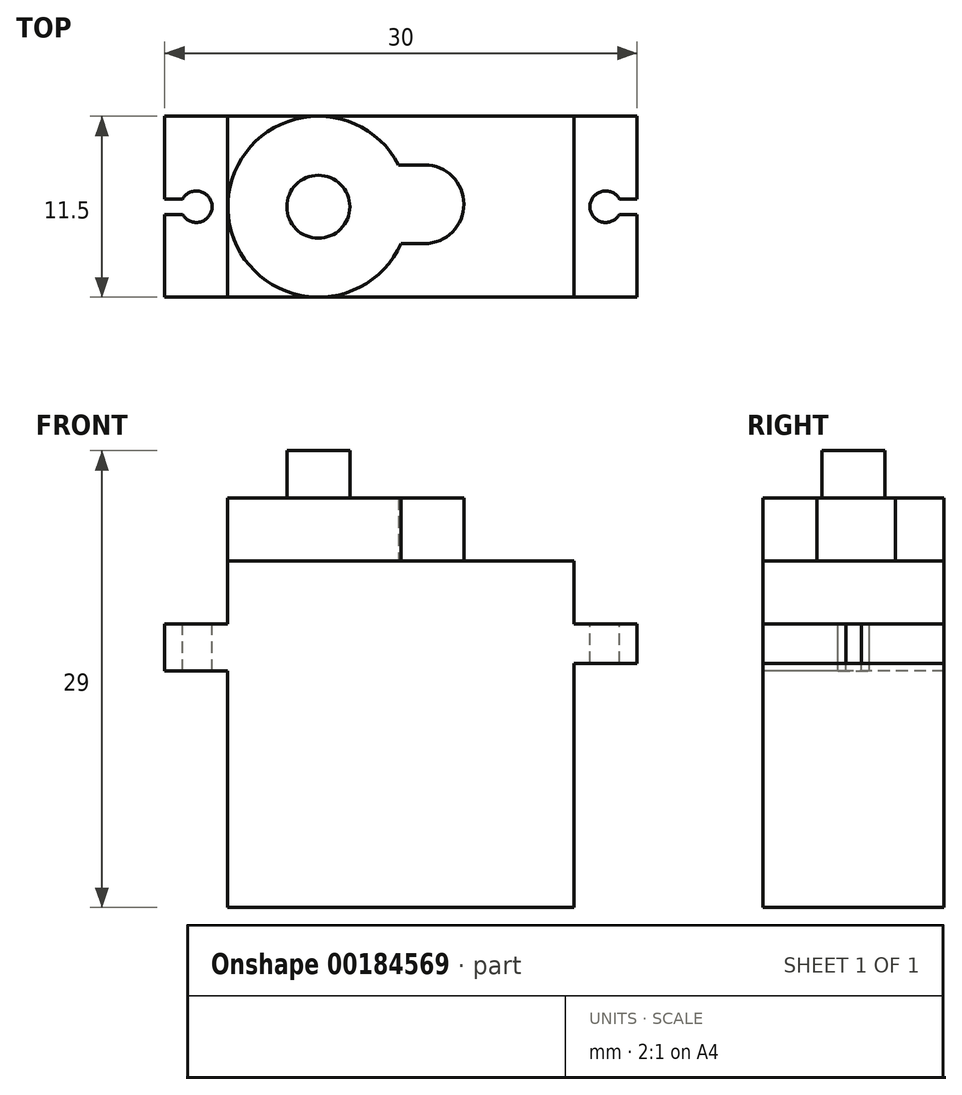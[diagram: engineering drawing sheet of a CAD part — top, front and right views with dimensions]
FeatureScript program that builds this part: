
annotation { "Feature Type Name" : "Feature", "Feature Type Description" : "" }
export const myFeature = defineFeature(function(context is Context, id is Id, definition is map)
    precondition{}
    {
        {
            var Q0;
            Q0=qCreatedBy(makeId("Front.planeOp"),FACE);
            var sketch = newSketch(context, id + "F0", { "sketchPlane" : qUnion([Q0])});
            skLineSegment(sketch, "E0.bottom", {"start": v(0, 0) * mm, "end": v(-22, 0) * mm});
            skLineSegment(sketch, "E0.top", {"start": v(0, 22) * mm, "end": v(-22, 22) * mm});
            skLineSegment(sketch, "E0.left", {"start": v(0, 0) * mm, "end": v(0, 22) * mm});
            skLineSegment(sketch, "E0.right", {"start": v(-22, 0) * mm, "end": v(-22, 22) * mm});
            skSolve(sketch);
        }
        {
            var Q0;
            Q0=makeQuery(id+"F0.imprint","IMPRINT",FACE,{"disambiguationData":[TD([[makeQuery(id+"F0.imprint","IMPRINT",EDGE,{"derivedFrom":sQuery(id+"F0.wireOp",EDGE,"E0.bottom")}),-1.0]])]});
            extrude(context, id + "F1", {"entities" : qUnion([Q0]), "depth" : 11.5 * mm});
        }
        {
            var Q0;
            Q0=makeQuery(id+"F1.opExtrude","SWEPT_FACE",FACE,{"disambiguationData":[OSD([sQuery(id+"F0.wireOp",EDGE,"E0.top")])]});
            var sketch = newSketch(context, id + "F2", { "sketchPlane" : qUnion([Q0])});
            skCircle(sketch, "E1", {"center": v(-16.25, -5.75) * mm, "radius": 5.75 * mm});
            skCircle(sketch, "E2", {"center": v(-9.5, -5.59) * mm, "radius": 2.5 * mm});
            skLineSegment(sketch, "E3", {"start": v(-9.5, -3.09) * mm, "end": v(-11.15, -3.09) * mm});
            skLineSegment(sketch, "E4", {"start": v(-9.5, -8.09) * mm, "end": v(-11, -8.09) * mm});
            skSolve(sketch);
        }
        {
            var Q0;
            {var subQ0=sQuery(id+"F2.wireOp",EDGE,"E1");var subQ5=makeQuery(id+"F2.imprint","INTERSECT",VERTEX,{"derivedFrom":[subQ0,sQuery(id+"F2.wireOp",EDGE,"E3")]});Q0=makeQuery(id+"F2.imprint","IMPRINT",FACE,{"disambiguationData":[TD([[makeQuery(id+"F2.imprint","IMPRINT",EDGE,{"disambiguationData":[TD([[subQ5,1.0]])],"derivedFrom":subQ0}),1.0]])]});}
            var Q1;
            {var subQ0=sQuery(id+"F2.wireOp",EDGE,"E2");var subQ1=sQuery(id+"F2.wireOp",EDGE,"E1");var subQ2=makeQuery(id+"F2.imprint","INTERSECT",VERTEX,{"disambiguationData":[OD(0.0)],"derivedFrom":[subQ1,subQ0]});Q1=makeQuery(id+"F2.imprint","IMPRINT",FACE,{"disambiguationData":[TD([[makeQuery(id+"F2.imprint","IMPRINT",EDGE,{"disambiguationData":[TD([[subQ2,1.0]])],"derivedFrom":subQ1}),1.0]])]});}
            var Q2;
            {var subQ0=sQuery(id+"F2.wireOp",EDGE,"E2");var subQ1=sQuery(id+"F2.wireOp",EDGE,"E1");var subQ2=makeQuery(id+"F2.imprint","INTERSECT",VERTEX,{"disambiguationData":[OD(0.0)],"derivedFrom":[subQ1,subQ0]});Q2=makeQuery(id+"F2.imprint","IMPRINT",FACE,{"disambiguationData":[TD([[makeQuery(id+"F2.imprint","IMPRINT",EDGE,{"disambiguationData":[TD([[subQ2,1.0]])],"derivedFrom":subQ1}),-1.0]])]});}
            var Q3;
            {var subQ0=sQuery(id+"F2.wireOp",EDGE,"E3");Q3=makeQuery(id+"F2.imprint","IMPRINT",FACE,{"disambiguationData":[TD([[makeQuery(id+"F2.imprint","IMPRINT",EDGE,{"derivedFrom":subQ0}),1.0]])]});}
            var Q4;
            {var subQ0=sQuery(id+"F2.wireOp",EDGE,"E4");Q4=makeQuery(id+"F2.imprint","IMPRINT",FACE,{"disambiguationData":[TD([[makeQuery(id+"F2.imprint","IMPRINT",EDGE,{"derivedFrom":subQ0}),-1.0]])]});}
            extrude(context, id + "F3", {"entities" : qUnion([Q0, Q1, Q2, Q3, Q4]), "operationType" : NewBodyOperationType.ADD, "depth" : 4 * mm});
        }
        {
            var Q0;
            Q0=makeQuery(id+"F3.opExtrude","CAP_FACE",FACE,{"disambiguationData":[OSD([sQuery(id+"F2.wireOp",EDGE,"E1"),sQuery(id+"F2.wireOp",EDGE,"E2"),sQuery(id+"F2.wireOp",EDGE,"E3"),sQuery(id+"F2.wireOp",EDGE,"E4")])],"isStart":false});
            var sketch = newSketch(context, id + "F4", { "sketchPlane" : qUnion([Q0])});
            skCircle(sketch, "E5", {"center": v(-16.25, -5.75) * mm, "radius": 2 * mm});
            skSolve(sketch);
        }
        {
            var Q0;
            Q0=qSketchRegion(id+"F4",true);
            extrude(context, id + "F5", {"entities" : qUnion([Q0]), "operationType" : NewBodyOperationType.ADD, "depth" : 3 * mm});
        }
        {
            var Q0;
            Q0=makeQuery(id+"F1.opExtrude","SWEPT_FACE",FACE,{"disambiguationData":[OSD([sQuery(id+"F0.wireOp",EDGE,"E0.left")])]});
            var sketch = newSketch(context, id + "F6", { "sketchPlane" : qUnion([Q0])});
            skLineSegment(sketch, "E6.bottom", {"start": v(-11.5, 18) * mm, "end": v(0, 18) * mm});
            skLineSegment(sketch, "E6.top", {"start": v(-11.5, 15.5) * mm, "end": v(0, 15.5) * mm});
            skLineSegment(sketch, "E6.left", {"start": v(-11.5, 18) * mm, "end": v(-11.5, 15.5) * mm});
            skLineSegment(sketch, "E6.right", {"start": v(0, 18) * mm, "end": v(0, 15.5) * mm});
            skSolve(sketch);
        }
        {
            var Q0;
            Q0=makeQuery(id+"F6.imprint","IMPRINT",FACE,{"disambiguationData":[TD([[makeQuery(id+"F6.imprint","IMPRINT",EDGE,{"derivedFrom":sQuery(id+"F6.wireOp",EDGE,"E6.bottom")}),-1.0]])]});
            extrude(context, id + "F7", {"entities" : qUnion([Q0]), "operationType" : NewBodyOperationType.ADD, "depth" : 4 * mm});
        }
        {
            var Q0;
            Q0=makeQuery(id+"F1.opExtrude","SWEPT_FACE",FACE,{"disambiguationData":[OSD([sQuery(id+"F0.wireOp",EDGE,"E0.right")])]});
            var sketch = newSketch(context, id + "F8", { "sketchPlane" : qUnion([Q0])});
            skLineSegment(sketch, "E7.bottom", {"start": v(0, 15) * mm, "end": v(11.5, 15) * mm});
            skLineSegment(sketch, "E7.top", {"start": v(0, 18) * mm, "end": v(11.5, 18) * mm});
            skLineSegment(sketch, "E7.left", {"start": v(0, 15) * mm, "end": v(0, 18) * mm});
            skLineSegment(sketch, "E7.right", {"start": v(11.5, 15) * mm, "end": v(11.5, 18) * mm});
            skSolve(sketch);
        }
        {
            var Q0;
            Q0=makeQuery(id+"F8.imprint","IMPRINT",FACE,{"disambiguationData":[TD([[makeQuery(id+"F8.imprint","IMPRINT",EDGE,{"derivedFrom":sQuery(id+"F8.wireOp",EDGE,"E7.bottom")}),1.0]])]});
            extrude(context, id + "F9", {"entities" : qUnion([Q0]), "operationType" : NewBodyOperationType.ADD, "depth" : 4 * mm});
        }
        {
            var Q0;
            Q0=makeQuery(id+"F9.opExtrude","SWEPT_FACE",FACE,{"disambiguationData":[OSD([sQuery(id+"F8.wireOp",EDGE,"E7.top")])]});
            var sketch = newSketch(context, id + "F10", { "sketchPlane" : qUnion([Q0])});
            skCircle(sketch, "E8", {"center": v(-24, -5.75) * mm, "radius": 1 * mm});
            skPoint(sketch, "E8.centerSnap0", {"position": v(-26, -5.75) * mm});
            skLineSegment(sketch, "E9", {"start": v(-24.87, -5.25) * mm, "end": v(-26, -5.25) * mm});
            skLineSegment(sketch, "E10", {"start": v(-24.87, -6.25) * mm, "end": v(-26, -6.25) * mm});
            skSolve(sketch);
        }
        {
            var Q0;
            {var subQ0=sQuery(id+"F10.wireOp",EDGE,"E8");var subQ1=makeQuery(id+"F10.imprint","INTERSECT",VERTEX,{"derivedFrom":[subQ0,sQuery(id+"F10.wireOp",EDGE,"E9")]});Q0=makeQuery(id+"F10.imprint","IMPRINT",FACE,{"disambiguationData":[TD([[makeQuery(id+"F10.imprint","IMPRINT",EDGE,{"disambiguationData":[TD([[subQ1,-1.0]])],"derivedFrom":subQ0}),1.0]])]});}
            var Q1;
            {var subQ0=sQuery(id+"F10.wireOp",EDGE,"E9");Q1=makeQuery(id+"F10.imprint","IMPRINT",FACE,{"disambiguationData":[TD([[makeQuery(id+"F10.imprint","IMPRINT",EDGE,{"derivedFrom":subQ0}),1.0]])]});}
            extrude(context, id + "F11", {"entities" : qUnion([Q0, Q1]), "operationType" : NewBodyOperationType.REMOVE, "oppositeDirection" : true, "depth" : 25.4 * mm});
        }
        {
            var Q0;
            Q0=makeQuery(id+"F7.opExtrude","SWEPT_FACE",FACE,{"disambiguationData":[OSD([sQuery(id+"F6.wireOp",EDGE,"E6.bottom")])]});
            var sketch = newSketch(context, id + "F12", { "sketchPlane" : qUnion([Q0])});
            skCircle(sketch, "E11", {"center": v(2, -5.75) * mm, "radius": 1 * mm});
            skPoint(sketch, "E11.centerSnap0", {"position": v(4, -5.75) * mm});
            skLineSegment(sketch, "E12", {"start": v(2.87, -6.25) * mm, "end": v(4, -6.25) * mm});
            skLineSegment(sketch, "E13", {"start": v(2.87, -5.25) * mm, "end": v(4, -5.25) * mm});
            skSolve(sketch);
        }
        {
            var Q0;
            {var subQ0=sQuery(id+"F12.wireOp",EDGE,"E11");var subQ1=makeQuery(id+"F12.imprint","INTERSECT",VERTEX,{"derivedFrom":[subQ0,sQuery(id+"F12.wireOp",EDGE,"E12")]});Q0=makeQuery(id+"F12.imprint","IMPRINT",FACE,{"disambiguationData":[TD([[makeQuery(id+"F12.imprint","IMPRINT",EDGE,{"disambiguationData":[TD([[subQ1,1.0]])],"derivedFrom":subQ0}),1.0]])]});}
            var Q1;
            {var subQ0=sQuery(id+"F12.wireOp",EDGE,"E12");Q1=makeQuery(id+"F12.imprint","IMPRINT",FACE,{"disambiguationData":[TD([[makeQuery(id+"F12.imprint","IMPRINT",EDGE,{"derivedFrom":subQ0}),1.0]])]});}
            extrude(context, id + "F13", {"entities" : qUnion([Q0, Q1]), "operationType" : NewBodyOperationType.REMOVE, "oppositeDirection" : true, "depth" : 25.4 * mm});
        }
    });
